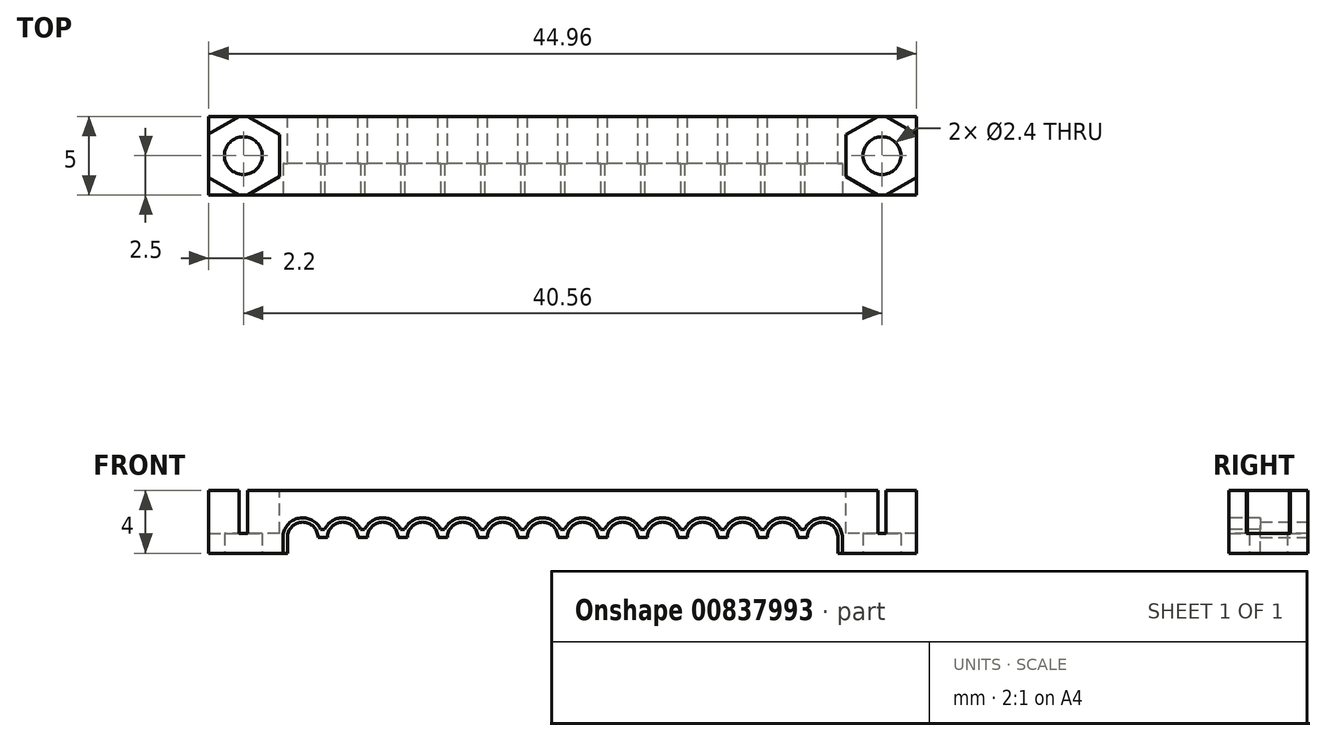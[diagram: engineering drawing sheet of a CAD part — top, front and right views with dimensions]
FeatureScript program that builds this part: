
annotation { "Feature Type Name" : "Feature", "Feature Type Description" : "" }
export const myFeature = defineFeature(function(context is Context, id is Id, definition is map)
    precondition{}
    {
        {
            var Q0;
            Q0=qCreatedBy(makeId("Front.planeOp"),FACE);
            var sketch = newSketch(context, id + "F0", { "sketchPlane" : qUnion([Q0])});
            skCircle(sketch, "E0", {"center": v(-1.27, 1.27) * mm, "radius": 0.97 * mm});
            skCircle(sketch, "E1", {"center": v(1.27, 1.27) * mm, "radius": 0.97 * mm});
            skCircle(sketch, "E2", {"center": v(3.8, 1.27) * mm, "radius": 0.97 * mm});
            skCircle(sketch, "E3", {"center": v(6.35, 1.27) * mm, "radius": 0.97 * mm});
            skCircle(sketch, "E4", {"center": v(8.9, 1.27) * mm, "radius": 0.97 * mm});
            skCircle(sketch, "E5", {"center": v(11.43, 1.27) * mm, "radius": 0.97 * mm});
            skCircle(sketch, "E6", {"center": v(13.97, 1.27) * mm, "radius": 0.97 * mm});
            skCircle(sketch, "E7", {"center": v(16.51, 1.27) * mm, "radius": 0.97 * mm});
            skCircle(sketch, "E8", {"center": v(-3.8, 1.27) * mm, "radius": 0.97 * mm});
            skCircle(sketch, "E9", {"center": v(-6.35, 1.27) * mm, "radius": 0.97 * mm});
            skCircle(sketch, "E10", {"center": v(-8.9, 1.27) * mm, "radius": 0.97 * mm});
            skCircle(sketch, "E11", {"center": v(-11.43, 1.27) * mm, "radius": 0.97 * mm});
            skCircle(sketch, "E12", {"center": v(-13.97, 1.27) * mm, "radius": 0.97 * mm});
            skCircle(sketch, "E13", {"center": v(-16.51, 1.27) * mm, "radius": 0.97 * mm});
            skLineSegment(sketch, "E14.bottom", {"start": v(-22.48, 4.27) * mm, "end": v(22.48, 4.27) * mm});
            skLineSegment(sketch, "E14.top", {"start": v(-22.48, 1.27) * mm, "end": v(22.48, 1.27) * mm});
            skLineSegment(sketch, "E14.left", {"start": v(-22.48, 4.27) * mm, "end": v(-22.48, 1.27) * mm});
            skLineSegment(sketch, "E14.right", {"start": v(22.48, 4.27) * mm, "end": v(22.48, 1.27) * mm});
            skSolve(sketch);
        }
        {
            var Q0;
            Q0=makeQuery(id+"F0.imprint","IMPRINT",FACE,{"disambiguationData":[TD([[makeQuery(id+"F0.imprint","IMPRINT",EDGE,{"derivedFrom":sQuery(id+"F0.wireOp",EDGE,"E14.bottom")}),-1.0]])]});
            extrude(context, id + "F1", {"entities" : qUnion([Q0]), "depth" : 5 * mm, "offsetDistance" : 25 * mm});
        }
        {
            var Q0;
            Q0=makeQuery(id+"F1.opExtrude","CAP_FACE",FACE,{"disambiguationData":[OSD([sQuery(id+"F0.wireOp",EDGE,"E0"),sQuery(id+"F0.wireOp",EDGE,"E1"),sQuery(id+"F0.wireOp",EDGE,"E2"),sQuery(id+"F0.wireOp",EDGE,"E3"),sQuery(id+"F0.wireOp",EDGE,"E4"),sQuery(id+"F0.wireOp",EDGE,"E5"),sQuery(id+"F0.wireOp",EDGE,"E6"),sQuery(id+"F0.wireOp",EDGE,"E7"),sQuery(id+"F0.wireOp",EDGE,"E8"),sQuery(id+"F0.wireOp",EDGE,"E9"),sQuery(id+"F0.wireOp",EDGE,"E10"),sQuery(id+"F0.wireOp",EDGE,"E11"),sQuery(id+"F0.wireOp",EDGE,"E12"),sQuery(id+"F0.wireOp",EDGE,"E13"),sQuery(id+"F0.wireOp",EDGE,"E14.bottom"),sQuery(id+"F0.wireOp",EDGE,"E14.top"),sQuery(id+"F0.wireOp",EDGE,"E14.left"),sQuery(id+"F0.wireOp",EDGE,"E14.right")])],"isStart":false});
            var sketch = newSketch(context, id + "F2", { "sketchPlane" : qUnion([Q0])});
            skCircle(sketch, "E15", {"center": v(-16.51, 1.27) * mm, "radius": 1.25 * mm});
            skCircle(sketch, "E16", {"center": v(-13.97, 1.27) * mm, "radius": 1.25 * mm});
            skCircle(sketch, "E17", {"center": v(-11.43, 1.27) * mm, "radius": 1.25 * mm});
            skCircle(sketch, "E18", {"center": v(-8.9, 1.27) * mm, "radius": 1.25 * mm});
            skCircle(sketch, "E19", {"center": v(-6.35, 1.27) * mm, "radius": 1.25 * mm});
            skCircle(sketch, "E20", {"center": v(-3.8, 1.27) * mm, "radius": 1.25 * mm});
            skCircle(sketch, "E21", {"center": v(-1.27, 1.27) * mm, "radius": 1.25 * mm});
            skCircle(sketch, "E22", {"center": v(1.27, 1.27) * mm, "radius": 1.25 * mm});
            skCircle(sketch, "E23", {"center": v(3.8, 1.27) * mm, "radius": 1.25 * mm});
            skCircle(sketch, "E24", {"center": v(6.35, 1.27) * mm, "radius": 1.25 * mm});
            skCircle(sketch, "E25", {"center": v(8.9, 1.27) * mm, "radius": 1.25 * mm});
            skCircle(sketch, "E26", {"center": v(11.43, 1.27) * mm, "radius": 1.25 * mm});
            skCircle(sketch, "E27", {"center": v(13.97, 1.27) * mm, "radius": 1.25 * mm});
            skCircle(sketch, "E28", {"center": v(16.51, 1.27) * mm, "radius": 1.25 * mm});
            skLineSegment(sketch, "E29.bottom", {"start": v(-16.51, 1.27) * mm, "end": v(16.51, 1.27) * mm});
            skLineSegment(sketch, "E29.top", {"start": v(-16.51, 1.77) * mm, "end": v(16.51, 1.77) * mm});
            skLineSegment(sketch, "E29.left", {"start": v(-16.51, 1.27) * mm, "end": v(-16.51, 1.77) * mm});
            skLineSegment(sketch, "E29.right", {"start": v(16.51, 1.27) * mm, "end": v(16.51, 1.77) * mm});
            skSolve(sketch);
        }
        {
            var Q0;
            Q0 = qSketchRegion(id + "F2", true);
            extrude(context, id + "F3", {"entities" : qUnion([Q0]), "operationType" : NewBodyOperationType.REMOVE, "oppositeDirection" : true, "depth" : 2 * mm, "offsetDistance" : 25 * mm});
        }
        {
            var Q0;
            Q0=makeQuery(id+"F1.opExtrude","SWEPT_FACE",FACE,{"disambiguationData":[OSD([sQuery(id+"F0.wireOp",EDGE,"E14.bottom")])]});
            var sketch = newSketch(context, id + "F4", { "sketchPlane" : qUnion([Q0])});
            skCircle(sketch, "E30", {"center": v(20.28, -2.5) * mm, "radius": 2.3 * mm});
            skCircle(sketch, "E31", {"center": v(-20.28, -2.5) * mm, "radius": 2.3 * mm});
            skLineSegment(sketch, "E32", {"start": v(22.58, -3.83) * mm, "end": v(22.58, -1.17) * mm});
            skLineSegment(sketch, "E33", {"start": v(22.58, -1.17) * mm, "end": v(20.28, 0.16) * mm});
            skLineSegment(sketch, "E34", {"start": v(20.28, 0.16) * mm, "end": v(17.98, -1.17) * mm});
            skLineSegment(sketch, "E35", {"start": v(17.98, -1.17) * mm, "end": v(17.98, -3.83) * mm});
            skLineSegment(sketch, "E36", {"start": v(17.98, -3.83) * mm, "end": v(20.28, -5.16) * mm});
            skLineSegment(sketch, "E37", {"start": v(20.28, -5.16) * mm, "end": v(22.58, -3.83) * mm});
            skLineSegment(sketch, "E38", {"start": v(-22.58, -1.17) * mm, "end": v(-22.58, -3.83) * mm});
            skLineSegment(sketch, "E39", {"start": v(-22.58, -3.83) * mm, "end": v(-20.28, -5.16) * mm});
            skLineSegment(sketch, "E40", {"start": v(-20.28, -5.16) * mm, "end": v(-17.98, -3.83) * mm});
            skLineSegment(sketch, "E41", {"start": v(-17.98, -3.83) * mm, "end": v(-17.98, -1.17) * mm});
            skLineSegment(sketch, "E42", {"start": v(-17.98, -1.17) * mm, "end": v(-20.28, 0.16) * mm});
            skLineSegment(sketch, "E43", {"start": v(-20.28, 0.16) * mm, "end": v(-22.58, -1.17) * mm});
            skSolve(sketch);
        }
        {
            var Q0;
            Q0 = qSketchRegion(id + "F4", true);
            extrude(context, id + "F5", {"entities" : qUnion([Q0]), "operationType" : NewBodyOperationType.REMOVE, "oppositeDirection" : true, "depth" : 2.75 * mm, "offsetDistance" : 25 * mm});
        }
        {
            var Q0;
            Q0=qCreatedBy(makeId("Top.planeOp"),FACE);
            var sketch = newSketch(context, id + "F6", { "sketchPlane" : qUnion([Q0])});
            skCircle(sketch, "E44", {"center": v(-20.28, -2.5) * mm, "radius": 1.2 * mm});
            skCircle(sketch, "E45", {"center": v(20.28, -2.5) * mm, "radius": 1.2 * mm});
            skSolve(sketch);
        }
        {
            var Q0;
            Q0=makeQuery(id+"F6.imprint","IMPRINT",FACE,{"disambiguationData":[TD([[makeQuery(id+"F6.imprint","IMPRINT",EDGE,{"derivedFrom":sQuery(id+"F6.wireOp",EDGE,"E44")}),1.0]])]});
            var Q1;
            Q1=makeQuery(id+"F6.imprint","IMPRINT",FACE,{"disambiguationData":[TD([[makeQuery(id+"F6.imprint","IMPRINT",EDGE,{"derivedFrom":sQuery(id+"F6.wireOp",EDGE,"E45")}),1.0]])]});
            extrude(context, id + "F7", {"entities" : qUnion([Q0, Q1]), "operationType" : NewBodyOperationType.REMOVE, "oppositeDirection" : true, "depth" : -5 * mm, "offsetDistance" : 25 * mm});
        }
        {
            var Q0;
            {var subQ0=sQuery(id+"F0.wireOp",EDGE,"E14.top");Q0=makeQuery(id+"F1.opExtrude","SWEPT_FACE",FACE,{"disambiguationData":[OSD([subQ0]),TDD([makeQuery(id+"F0.imprint","IMPRINT",EDGE,{"disambiguationData":[TD([[makeQuery(id+"F0.imprint","INTERSECT",VERTEX,{"derivedFrom":[subQ0,sQuery(id+"F0.wireOp",EDGE,"E14.left")]}),-1.0]])],"derivedFrom":subQ0})])]});}
            var Q1;
            {var subQ0=sQuery(id+"F0.wireOp",EDGE,"E14.top");Q1=makeQuery(id+"F1.opExtrude","SWEPT_FACE",FACE,{"disambiguationData":[OSD([subQ0]),TDD([makeQuery(id+"F0.imprint","IMPRINT",EDGE,{"disambiguationData":[TD([[makeQuery(id+"F0.imprint","INTERSECT",VERTEX,{"derivedFrom":[subQ0,sQuery(id+"F0.wireOp",EDGE,"E14.right")]}),1.0]])],"derivedFrom":subQ0})])]});}
            extrude(context, id + "F8", {"entities" : qUnion([Q0, Q1]), "operationType" : NewBodyOperationType.ADD, "depth" : 1 * mm, "offsetDistance" : 25 * mm});
        }
    });
